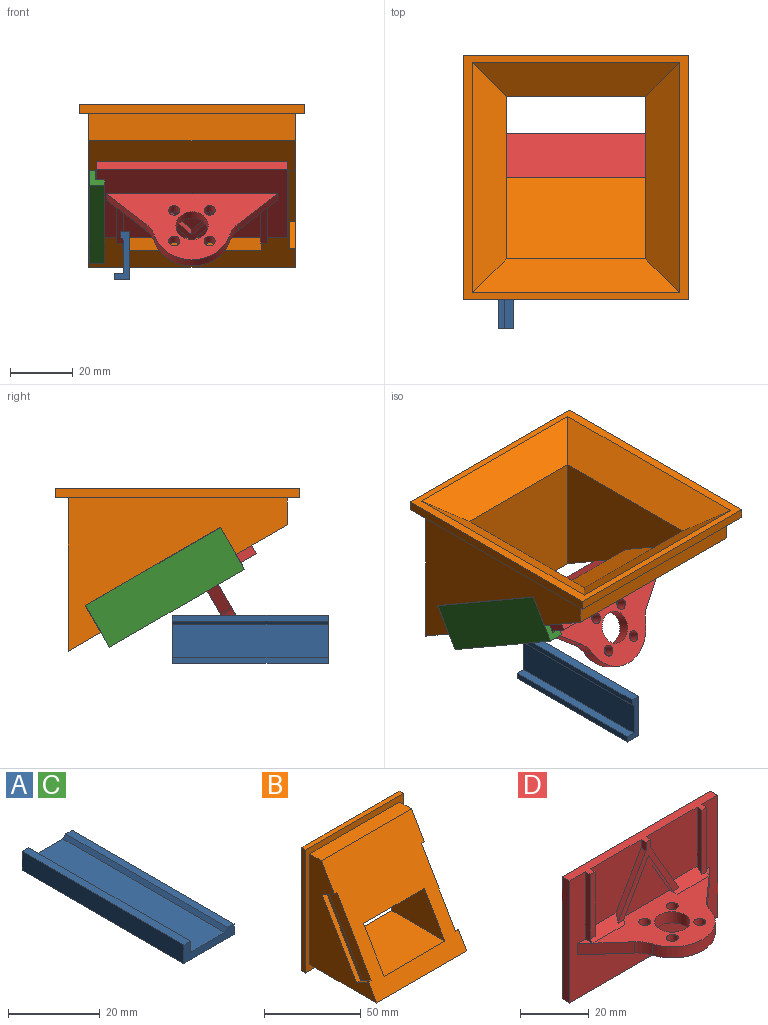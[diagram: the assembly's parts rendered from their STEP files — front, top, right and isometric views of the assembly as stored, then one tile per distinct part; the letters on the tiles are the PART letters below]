
ASSEMBLY  parts=4 mates=2
PART A: 10 faces, bbox 15.4x49.8x5 mm
  f0: plane 49.8x10.6mm, normal (0,0,1), area 527.9mm2, adj f1,f3,f7,f8
  f1: plane 15.4x5mm, normal (0,-1,0), area 38.9mm2, adj f0,f2,f4,f5,f6,f7,f8,f9
  f2: plane 49.8x2.9mm, normal (1,0,0), area 144.4mm2, adj f1,f3,f5,f6
  f3: plane 15.4x5mm, normal (0,1,0), area 38.9mm2, adj f0,f2,f4,f5,f6,f7,f8,f9
  f4: plane 49.8x5mm, normal (-1,0,0), area 249mm2, adj f1,f3,f5,f9
  f5: plane 49.8x15.4mm, normal (0,0,-1), area 766.9mm2, adj f1,f2,f3,f4
  f6: plane 49.8x1.9mm, normal (0,0,1), area 94.6mm2, adj f1,f2,f3,f7
  f7: plane 49.8x0.9mm, normal (-0.71,0,0.71), area 63.4mm2, adj f0,f1,f3,f6
  f8: plane 49.8x3mm, normal (1,0,0), area 149.4mm2, adj f0,f1,f3,f9
  f9: plane 49.8x2mm, normal (0,0,1), area 99.6mm2, adj f1,f3,f4,f8
PART B: 33 faces, bbox 72x52x78 mm
  f0: plane 52x38.8mm, normal (-1,0,0), area 1147.1mm2, adj f1,f4,f5,f26,f29,f30
  f1: plane 70x66mm, normal (0,-0.87,0.5), area 3796.7mm2, adj f0,f2,f3,f5,f6,f11,f12,f13
  f2: plane 70x49mm, normal (1,0,0), area 1515.5mm2, adj f1,f3,f9,f12,f13,f14,f15
  f3: plane 66x8.59mm, normal (0,0,1), area 566.6mm2, adj f1,f2,f9,f11
  f4: plane 44.6x5.32mm, normal (0,0,-1), area 237.2mm2, adj f0,f6,f28,f29
  f5: plane 44.6x38.8mm, normal (0,0,1), area 1730.7mm2, adj f0,f1,f6,f25
  f6: plane 52x38.8mm, normal (1,0,0), area 1147.1mm2, adj f1,f4,f5,f27,f29,f30
  f7: plane 78x3mm, normal (1,0,0), area 234mm2, adj f9,f10,f31,f32
  f8: plane 78x3mm, normal (-1,0,0), area 234mm2, adj f9,f10,f31,f32
  f9: plane 78x72mm, normal (0,-1,0), area 996mm2, adj f2,f3,f7,f8,f11,f12,f31,f32
  f10: plane 78x72mm, normal (0,1,0), area 743.7mm2, adj f7,f8,f25,f26,f27,f28,f31,f32
  f11: plane 70x49mm, normal (-1,0,0), area 1515.5mm2, adj f1,f3,f9,f12,f17,f18,f19
  f12: plane 66x49mm, normal (0,0,-1), area 3234mm2, adj f1,f2,f9,f11
  f13: plane 8.66x5mm, normal (0,0.5,0.87), area 22.6mm2, adj f1,f2,f14,f16,f22,f24
  f14: plane 43.3x25mm, normal (0,-0.87,0.5), area 150mm2, adj f2,f13,f15,f22
  f15: plane 8.66x5mm, normal (0,-0.5,-0.87), area 22.6mm2, adj f1,f2,f14,f16,f22,f24
  f16: plane 46.75x30.98mm, normal (1,0,0), area 345mm2, adj f1,f13,f15,f24
  f17: plane 8.66x5mm, normal (0,0.5,0.87), area 22.6mm2, adj f1,f11,f19,f20,f21,f23
  f18: plane 8.66x5mm, normal (0,-0.5,-0.87), area 22.6mm2, adj f1,f11,f19,f20,f21,f23
  f19: plane 43.3x25mm, normal (0,-0.87,0.5), area 150mm2, adj f11,f17,f18,f21
  f20: plane 46.75x30.98mm, normal (-1,0,0), area 345mm2, adj f1,f17,f18,f23
  f21: plane 44.35x26.82mm, normal (-1,0,0), area 105mm2, adj f17,f18,f19,f23
  f22: plane 44.35x26.82mm, normal (1,0,0), area 105mm2, adj f13,f14,f15,f24
  f23: plane 43.8x25.87mm, normal (-0.71,0.61,-0.35), area 70.7mm2, adj f17,f18,f20,f21
  f24: plane 43.8x25.87mm, normal (0.71,0.61,-0.35), area 70.7mm2, adj f13,f15,f16,f22
  f25: plane 66.2x10.8mm, normal (0,0.8,0.6), area 744.6mm2, adj f5,f10,f26,f27
  f26: plane 73.6x10.8mm, normal (-0.6,0.8,0), area 844mm2, adj f0,f10,f25,f28
  f27: plane 73.6x10.8mm, normal (0.6,0.8,0), area 844mm2, adj f6,f10,f25,f28
  f28: plane 66.2x10.8mm, normal (0,0.8,-0.6), area 744.6mm2, adj f4,f10,f26,f27
  f29: plane 44.6x26.02mm, normal (0,0.87,-0.5), area 1340mm2, adj f0,f4,f6,f30
  f30: plane 44.6x3.46mm, normal (0,0,-1), area 154.5mm2, adj f0,f1,f6,f29
  f31: plane 72x3mm, normal (0,0,1), area 216mm2, adj f7,f8,f9,f10
  f32: plane 72x3mm, normal (0,0,-1), area 216mm2, adj f7,f8,f9,f10
PART C: same geometry as A
PART D: 38 faces, bbox 61.2x27.3x43.5 mm
  f0: plane 43.5x3mm, normal (1,0,0), area 130.5mm2, adj f1,f4,f36,f37
  f1: plane 61.2x43.5mm, normal (0,1,0), area 2662.2mm2, adj f0,f2,f36,f37
  f2: plane 43.5x3mm, normal (-1,0,0), area 130.5mm2, adj f1,f4,f36,f37
  f3: plane 21x21mm, normal (0,-1,0), area 347.5mm2, adj f9,f11,f31,f35,f37
  f4: plane 61.2x43.5mm, normal (0,-1,0), area 1291.7mm2, adj f0,f2,f6,f10,f13,f15,f22,f23
  f5: plane 21x21mm, normal (0,-1,0), area 347.5mm2, adj f7,f8,f28,f34,f37
  f6: plane 24x2.95mm, normal (-1,0,0), area 48.5mm2, adj f4,f13,f24,f27,f34,f37
  f7: plane 23x2mm, normal (1,0,0), area 44mm2, adj f5,f27,f34,f37
  f8: plane 3x2mm, normal (-1,0,0), area 6mm2, adj f5,f28,f32,f37
  f9: plane 3x2mm, normal (1,0,0), area 6mm2, adj f3,f31,f32,f37
  f10: plane 24x2.95mm, normal (1,0,0), area 48.5mm2, adj f4,f15,f23,f33,f35,f37
  f11: plane 23x2mm, normal (-1,0,0), area 44mm2, adj f3,f33,f35,f37
  f12: plane 47.88x24.3mm, normal (0,0,1), area 526.8mm2, adj f14,f16,f17,f18,f19,f20,f21,f23
  f13: plane 3.31x2.95mm, normal (0,0,1), area 4.9mm2, adj f4,f6,f24
  f14: plane 21.63x18.73mm, normal (0,-1,0), area 202.6mm2, adj f12,f29,f30
  f15: plane 3.31x2.95mm, normal (0,0,1), area 4.9mm2, adj f4,f10,f23
  f16: cylinder r=12.5mm len=23.83mm, axis (0,0,-1), area 126.4mm2, adj f12,f22,f25,f26
  f17: cylinder r=1.75mm len=4mm, axis (0,0,-1), area 44mm2, adj f12,f22
  f18: cylinder r=1.75mm len=4mm, axis (0,0,-1), area 44mm2, adj f12,f22
  f19: cylinder r=1.75mm len=4mm, axis (0,0,-1), area 44mm2, adj f12,f22
  f20: cylinder r=1.75mm len=4mm, axis (0,0,-1), area 44mm2, adj f12,f22
  f21: cylinder r=5.15mm len=10.3mm, axis (0,0,-1), area 129.4mm2, adj f12,f22
  f22: plane 54.63x24.3mm, normal (0,0,-1), area 615.7mm2, adj f4,f16,f17,f18,f19,f20,f21,f23
  f23: plane 12.51x11.13mm, normal (0.66,-0.75,0), area 67mm2, adj f4,f10,f12,f15,f22,f25,f35
  f24: plane 12.51x11.13mm, normal (-0.66,-0.75,0), area 67mm2, adj f4,f6,f12,f13,f22,f26,f34
  f25: cylinder r=10mm len=4.45mm, axis (0,0,-1), area 21.5mm2, adj f12,f16,f22,f23
  f26: cylinder r=10mm len=4.45mm, axis (0,0,-1), area 21.5mm2, adj f12,f16,f22,f24
  f27: plane 23x2mm, normal (0,-1,0), area 46mm2, adj f6,f7,f34,f37
  f28: plane 20x11.55mm, normal (-0.87,0,0.5), area 43.9mm2, adj f5,f8,f32,f34
  f29: plane 18.73x10.82mm, normal (0.87,0,-0.5), area 43.8mm2, adj f12,f14,f30,f32,f34
  f30: plane 18.73x10.82mm, normal (-0.87,0,-0.5), area 43.8mm2, adj f12,f14,f29,f32,f35
  f31: plane 20x11.55mm, normal (0.87,0,0.5), area 43.9mm2, adj f3,f9,f32,f35
  f32: plane 25.09x23mm, normal (0,-1,0), area 95.4mm2, adj f8,f9,f28,f29,f30,f31,f34,f35
  f33: plane 23x2mm, normal (0,-1,0), area 46mm2, adj f10,f11,f35,f37
  f34: plane 13.76x3mm, normal (0,-0.71,0.71), area 47.4mm2, adj f5,f6,f7,f12,f24,f27,f28,f29
  f35: plane 13.76x3mm, normal (0,-0.71,0.71), area 47.4mm2, adj f3,f10,f11,f12,f23,f30,f31,f32
  f36: plane 61.2x3mm, normal (0,0,-1), area 183.6mm2, adj f0,f1,f2,f4
  f37: plane 61.2x5mm, normal (0,0,1), area 195.6mm2, adj f0,f1,f2,f3,f4,f5,f6,f7
PLACE A rot(axis=(0,-1,0),90deg) t=(-27.01,-94.57,-53.13)mm
PLACE B rot(axis=(1,0,0),90deg) t=(-7.09,-71.33,-4.91)mm
PLACE C rot(axis=(0.69,0.19,0.69),158.9deg) t=(-39.99,-67.27,-36.5)mm
PLACE D rot(axis=(0,0.87,0.5),180deg) t=(-7.09,-88.88,-43.66)mm
MATE revolute C.f6 <-> B.f21  axis (1,0,0) through (-37.09,-63.9,-30.66)mm
MATE fastened D.f1 <-> B.f1  axis (0,0.5,0.87) through (-7.09,-76.07,-33.97)mm
